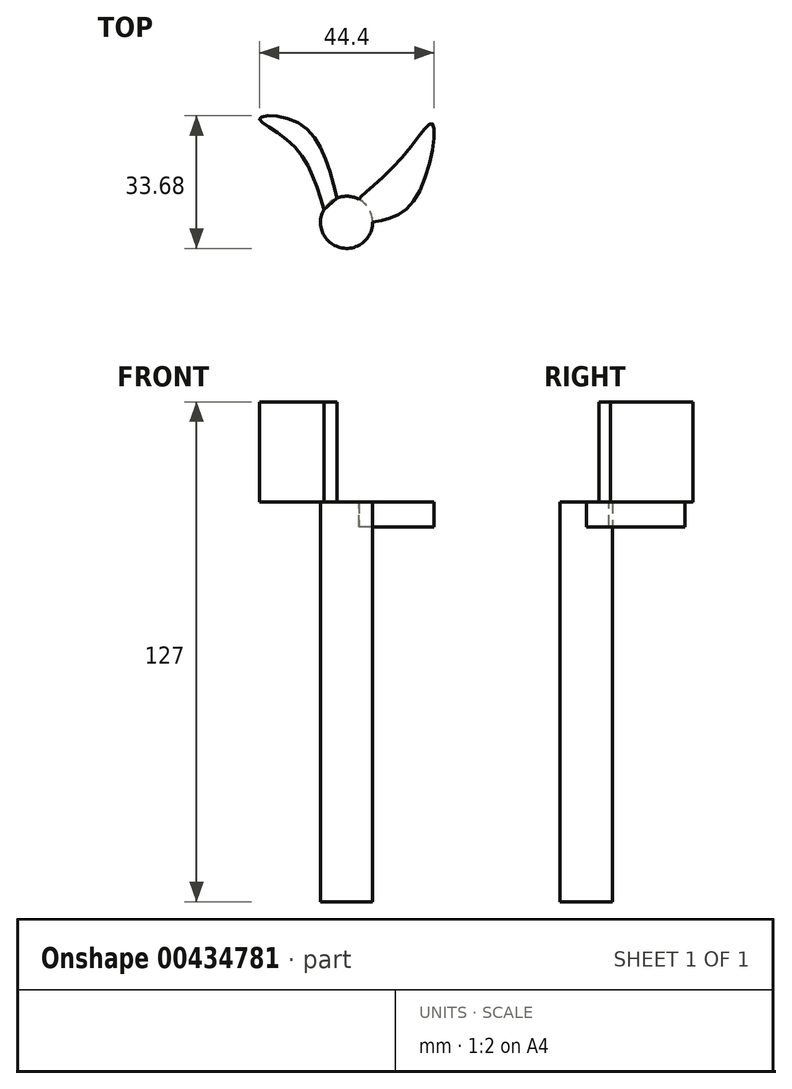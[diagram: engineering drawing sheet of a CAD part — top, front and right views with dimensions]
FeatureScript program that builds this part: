
annotation { "Feature Type Name" : "Feature", "Feature Type Description" : "" }
export const myFeature = defineFeature(function(context is Context, id is Id, definition is map)
    precondition{}
    {
        {
            var Q0;
            Q0=qCreatedBy(makeId("Top.planeOp"),FACE);
            var sketch = newSketch(context, id + "F0", { "sketchPlane" : qUnion([Q0])});
            skCircle(sketch, "E0", {"center": v(0, 0) * mm, "radius": 6.62 * mm});
            skSolve(sketch);
        }
        {
            var Q0;
            Q0 = qSketchRegion(id + "F0", true);
            extrude(context, id + "F1", {"entities" : qUnion([Q0]), "depth" : 101.6 * mm});
        }
        {
            var Q0;
            Q0=makeQuery(id+"F1.opExtrude","CAP_FACE",FACE,{"disambiguationData":[OSD([sQuery(id+"F0.wireOp",EDGE,"E0")])],"isStart":false});
            var sketch = newSketch(context, id + "F2", { "sketchPlane" : qUnion([Q0])});
            skFitSpline(sketch, "E1", {"points": [v(6.62, 0) * mm, v(17.6, 6.24) * mm, v(21.85, 24.97) * mm, v(13.33, 15.6) * mm, v(3.14, 5.83) * mm, v(3.4, 5.68) * mm], "startDerivative": vector(53.65, 10.56) * mm, "endDerivative": vector(10.9, -2.63) * mm});
            skFitSpline(sketch, "E2", {"points": [v(6.62, 0) * mm, v(3.4, 5.68) * mm], "startDerivative": vector(-3.22, 5.68) * mm, "endDerivative": vector(-3.22, 5.68) * mm});
            skSolve(sketch);
        }
        {
            var Q0;
            Q0 = qSketchRegion(id + "F2", true);
            extrude(context, id + "F3", {"entities" : qUnion([Q0]), "operationType" : NewBodyOperationType.ADD, "oppositeDirection" : true, "depth" : 6.35 * mm});
        }
        {
            var Q0;
            Q0=makeQuery(id+"F3.boolean.opBoolean","MERGE",FACE,{"derivedFrom":[makeQuery(id+"F1.opExtrude","CAP_FACE",FACE,{"disambiguationData":[OSD([sQuery(id+"F0.wireOp",EDGE,"E0")])],"isStart":false}),makeQuery(id+"F3.opExtrude","CAP_FACE",FACE,{"disambiguationData":[OSD([sQuery(id+"F2.wireOp",EDGE,"E1"),sQuery(id+"F2.wireOp",EDGE,"E2")])],"isStart":true})]});
            var sketch = newSketch(context, id + "F4", { "sketchPlane" : qUnion([Q0])});
            skFitSpline(sketch, "E3", {"points": [v(-2.39, 6.18) * mm, v(-12.2, 25.25) * mm, v(-22.13, 26.39) * mm, v(-14.19, 20.14) * mm, v(-5.8, 3.2) * mm], "startDerivative": vector(-20.22, 78.63) * mm, "endDerivative": vector(19.63, -66.82) * mm});
            skFitSpline(sketch, "E4", {"points": [v(-2.39, 6.18) * mm, v(-5.8, 3.2) * mm], "startDerivative": vector(-3.41, -2.98) * mm, "endDerivative": vector(-3.41, -2.98) * mm});
            skSolve(sketch);
        }
        {
            var Q0;
            Q0 = qSketchRegion(id + "F4", true);
            extrude(context, id + "F5", {"entities" : qUnion([Q0]), "operationType" : NewBodyOperationType.ADD, "depth" : 25.4 * mm});
        }
    });
